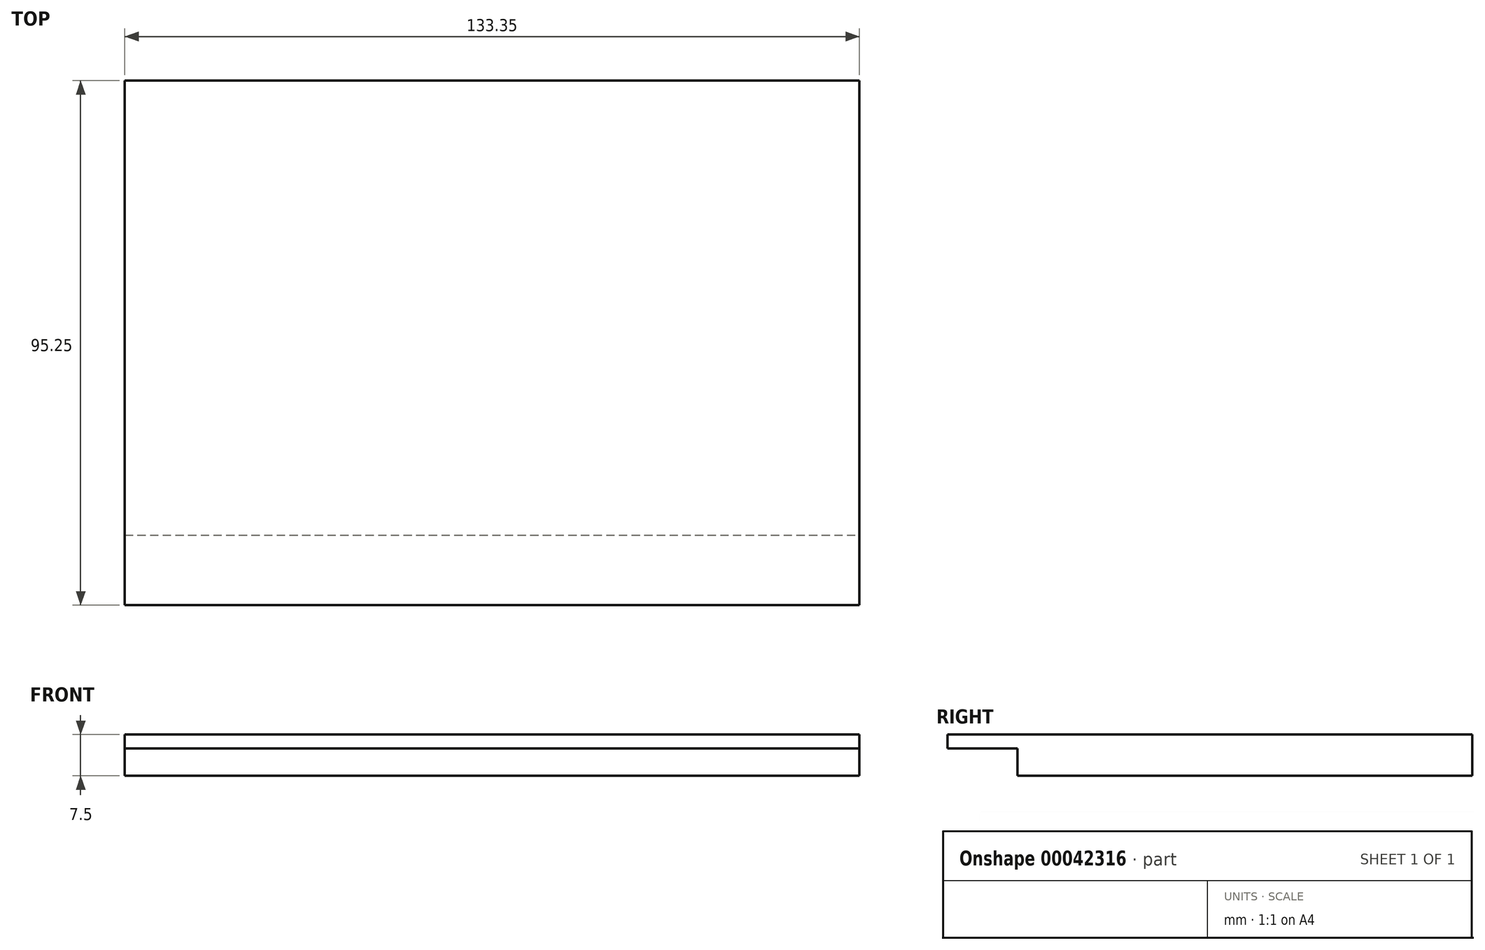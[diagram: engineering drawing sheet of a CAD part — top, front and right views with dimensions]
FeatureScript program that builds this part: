
annotation { "Feature Type Name" : "Feature", "Feature Type Description" : "" }
export const myFeature = defineFeature(function(context is Context, id is Id, definition is map)
    precondition{}
    {
        {
            var Q0;
            Q0=qCreatedBy(makeId("Top.planeOp"),FACE);
            var sketch = newSketch(context, id + "F0", { "sketchPlane" : qUnion([Q0])});
            skLineSegment(sketch, "E0.bottom", {"start": v(-48.28, 76.8) * mm, "end": v(85.07, 76.8) * mm});
            skLineSegment(sketch, "E0.top", {"start": v(-48.28, -31.14) * mm, "end": v(85.07, -31.14) * mm});
            skLineSegment(sketch, "E0.left", {"start": v(-48.28, 76.8) * mm, "end": v(-48.28, -31.14) * mm});
            skLineSegment(sketch, "E0.right", {"start": v(85.07, 76.8) * mm, "end": v(85.07, -31.14) * mm});
            skLineSegment(sketch, "E1.0", {"start": v(-45.1, 73.63) * mm, "end": v(81.9, 73.63) * mm});
            skLineSegment(sketch, "E1.1", {"start": v(-45.1, 73.63) * mm, "end": v(-45.1, -27.97) * mm});
            skLineSegment(sketch, "E1.2", {"start": v(-45.1, -27.97) * mm, "end": v(81.9, -27.97) * mm});
            skLineSegment(sketch, "E1.3", {"start": v(81.9, 73.63) * mm, "end": v(81.9, -27.97) * mm});
            skLineSegment(sketch, "E2", {"start": v(-48.28, -5.74) * mm, "end": v(85.07, -5.74) * mm});
            skPoint(sketch, "E3", {"position": v(-45.1, -5.74) * mm});
            skPoint(sketch, "E4", {"position": v(81.9, -5.74) * mm});
            skLineSegment(sketch, "E5", {"start": v(-48.28, -18.44) * mm, "end": v(85.07, -18.44) * mm});
            skPoint(sketch, "E6", {"position": v(-45.1, -18.44) * mm});
            skPoint(sketch, "E7", {"position": v(81.9, -18.44) * mm});
            skSolve(sketch);
        }
        {
            var Q0;
            {var subQ10=sQuery(id+"F0.wireOp",EDGE,"E0.bottom");Q0=makeQuery(id+"F0.imprint","IMPRINT",FACE,{"disambiguationData":[TD([[makeQuery(id+"F0.imprint","IMPRINT",EDGE,{"derivedFrom":subQ10}),-1.0]])]});}
            var Q1;
            {var subQ5=sQuery(id+"F0.wireOp",EDGE,"E1.0");Q1=makeQuery(id+"F0.imprint","IMPRINT",FACE,{"disambiguationData":[TD([[makeQuery(id+"F0.imprint","IMPRINT",EDGE,{"derivedFrom":subQ5}),-1.0]])]});}
            extrude(context, id + "F1", {"entities" : qUnion([Q0, Q1]), "oppositeDirection" : true, "depth" : 7.5 * mm});
        }
        {
            var Q0;
            {var subQ3=sQuery(id+"F0.wireOp",EDGE,"E0.left");var subQ5=sQuery(id+"F0.wireOp",EDGE,"E2");var subQ7=makeQuery(id+"F0.imprint","INTERSECT",VERTEX,{"derivedFrom":[subQ3,subQ5]});Q0=makeQuery(id+"F0.imprint","IMPRINT",FACE,{"disambiguationData":[TD([[makeQuery(id+"F0.imprint","IMPRINT",EDGE,{"disambiguationData":[TD([[subQ7,-1.0]])],"derivedFrom":subQ3}),1.0]])]});}
            var Q1;
            {var subQ0=sQuery(id+"F0.wireOp",EDGE,"E2");var subQ3=sQuery(id+"F0.wireOp",EDGE,"E0.right");var subQ4=makeQuery(id+"F0.imprint","INTERSECT",VERTEX,{"derivedFrom":[subQ3,subQ0]});Q1=makeQuery(id+"F0.imprint","IMPRINT",FACE,{"disambiguationData":[TD([[makeQuery(id+"F0.imprint","IMPRINT",EDGE,{"disambiguationData":[TD([[subQ4,-1.0]])],"derivedFrom":subQ3}),-1.0]])]});}
            var Q2;
            {var subQ3=sQuery(id+"F0.wireOp",EDGE,"E1.1");var subQ5=sQuery(id+"F0.wireOp",EDGE,"E2");var subQ7=makeQuery(id+"F0.imprint","INTERSECT",VERTEX,{"derivedFrom":[subQ3,subQ5]});Q2=makeQuery(id+"F0.imprint","IMPRINT",FACE,{"disambiguationData":[TD([[makeQuery(id+"F0.imprint","IMPRINT",EDGE,{"disambiguationData":[TD([[subQ7,-1.0]])],"derivedFrom":subQ3}),1.0]])]});}
            extrude(context, id + "F2", {"entities" : qUnion([Q0, Q1, Q2]), "operationType" : NewBodyOperationType.ADD, "oppositeDirection" : true, "depth" : 2.5 * mm});
        }
    });
